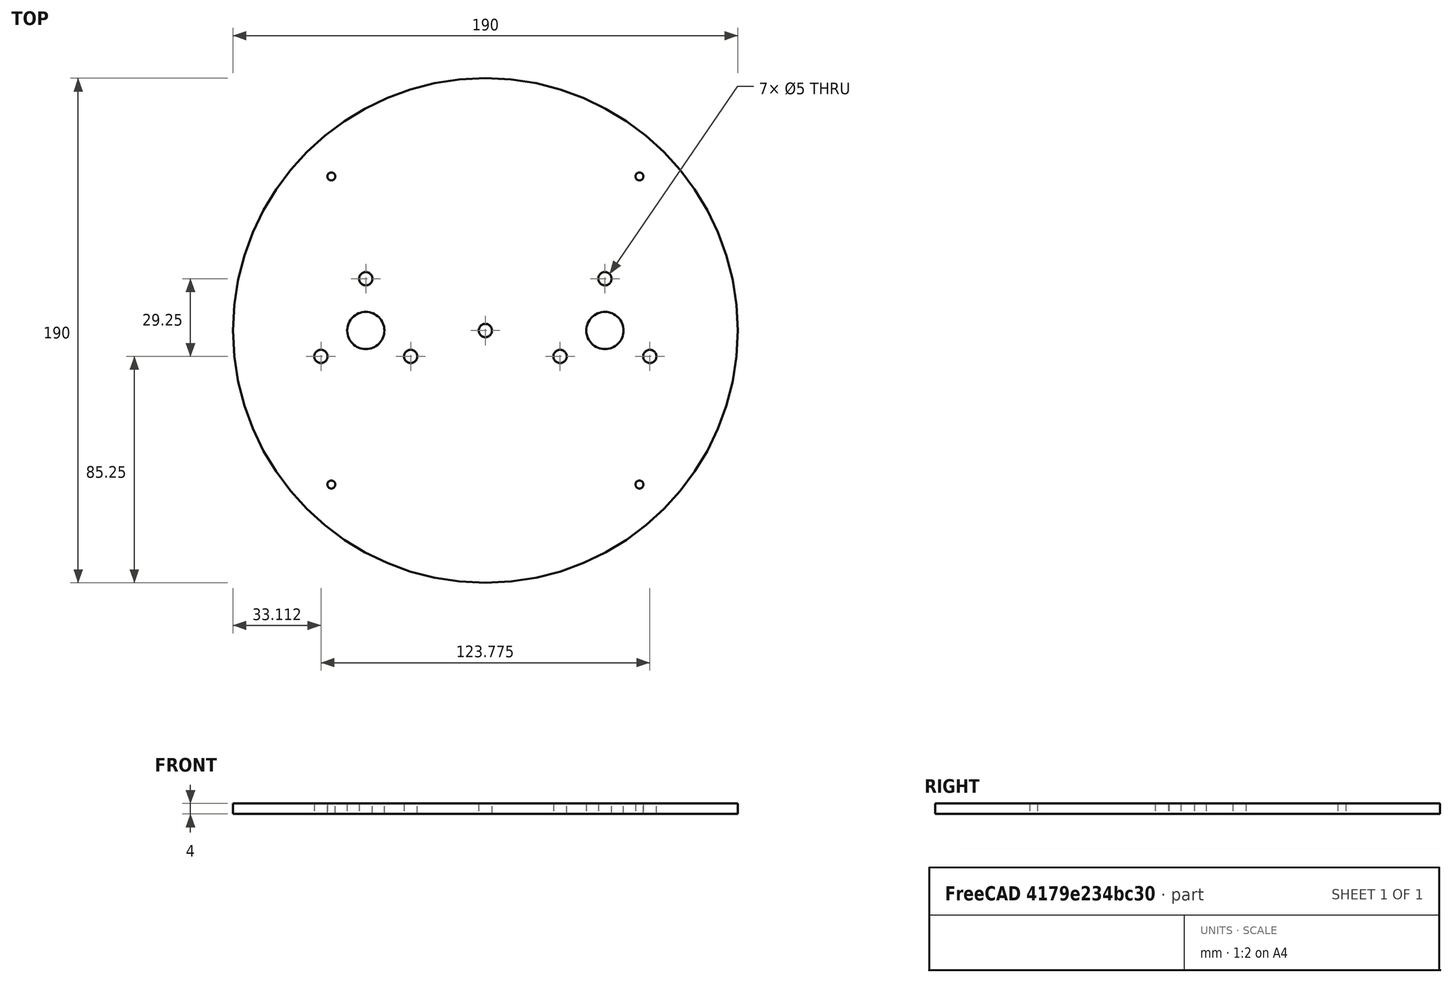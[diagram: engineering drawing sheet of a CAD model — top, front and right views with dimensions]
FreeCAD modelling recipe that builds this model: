
FCSTD DOCUMENT  (FreeCAD 0.19R24276 (Git))
Label: Osnovanie_karuseli
License: All rights reserved
LicenseURL: http://en.wikipedia.org/wiki/All_rights_reserved
objects: Sketcher::SketchObject×1, PartDesign::Pad×1, PartDesign::Body×1
note: 4 computed .brp shape members not serialized (recipe doc carries the construction recipe); baked Part::Feature solids carry a one-line shape summary decoded from their .brp

FEATURE [Sketcher::SketchObject] Sketch
  FullyConstrained = true
  MapMode = 5
  Support = -> [XY_Plane]
  sketch-geometry (27):
    g0: Circle CenterX=0 CenterY=0 CenterZ=0 NormalX=0 NormalY=0 NormalZ=1 AngleXU=0 Radius=95
    g1: Circle CenterX=-45 CenterY=0 CenterZ=0 NormalX=0 NormalY=0 NormalZ=1 AngleXU=0 Radius=7
    g2: Circle CenterX=45 CenterY=0 CenterZ=0 NormalX=0 NormalY=0 NormalZ=1 AngleXU=0 Radius=7
    g3: LineSegment StartX=0 StartY=0 StartZ=0 EndX=57.9828 EndY=57.9828 EndZ=0
    g4: LineSegment StartX=0 StartY=0 StartZ=0 EndX=-57.9828 EndY=57.9828 EndZ=0
    g5: LineSegment StartX=0 StartY=0 StartZ=0 EndX=-57.9828 EndY=-57.9828 EndZ=0
    g6: LineSegment StartX=0 StartY=0 StartZ=0 EndX=57.9828 EndY=-57.9828 EndZ=0
    g7: Circle CenterX=0 CenterY=0 CenterZ=0 NormalX=0 NormalY=0 NormalZ=1 AngleXU=0 Radius=82
    g8: Circle CenterX=57.9828 CenterY=57.9828 CenterZ=0 NormalX=0 NormalY=0 NormalZ=1 AngleXU=0 Radius=1.5
    g9: Circle CenterX=-57.9828 CenterY=57.9828 CenterZ=0 NormalX=0 NormalY=0 NormalZ=1 AngleXU=0 Radius=1.5
    g10: Circle CenterX=-57.9828 CenterY=-57.9828 CenterZ=0 NormalX=0 NormalY=0 NormalZ=1 AngleXU=0 Radius=1.5
    g11: Circle CenterX=57.9828 CenterY=-57.9828 CenterZ=0 NormalX=0 NormalY=0 NormalZ=1 AngleXU=0 Radius=1.5
    g12: LineSegment StartX=-45 StartY=19.5 StartZ=0 EndX=-61.8875 EndY=-9.75 EndZ=0
    g13: LineSegment StartX=-61.8875 StartY=-9.75 StartZ=0 EndX=-28.1125 EndY=-9.75 EndZ=0
    g14: LineSegment StartX=-28.1125 StartY=-9.75 StartZ=0 EndX=-45 EndY=19.5 EndZ=0
    g15: Circle CenterX=-45 CenterY=0 CenterZ=0 NormalX=0 NormalY=0 NormalZ=1 AngleXU=0 Radius=19.5
    g16: LineSegment StartX=45 StartY=19.5 StartZ=0 EndX=28.1125 EndY=-9.75 EndZ=0
    g17: LineSegment StartX=28.1125 StartY=-9.75 StartZ=0 EndX=61.8875 EndY=-9.75 EndZ=0
    g18: LineSegment StartX=61.8875 StartY=-9.75 StartZ=0 EndX=45 EndY=19.5 EndZ=0
    g19: Circle CenterX=45 CenterY=0 CenterZ=0 NormalX=0 NormalY=0 NormalZ=1 AngleXU=0 Radius=19.5
    g20: Circle CenterX=-45 CenterY=19.5 CenterZ=0 NormalX=0 NormalY=0 NormalZ=1 AngleXU=0 Radius=2.5
    g21: Circle CenterX=-28.1125 CenterY=-9.75 CenterZ=0 NormalX=0 NormalY=0 NormalZ=1 AngleXU=0 Radius=2.5
    g22: Circle CenterX=-61.8875 CenterY=-9.75 CenterZ=0 NormalX=0 NormalY=0 NormalZ=1 AngleXU=0 Radius=2.5
    g23: Circle CenterX=45 CenterY=19.5 CenterZ=0 NormalX=0 NormalY=0 NormalZ=1 AngleXU=0 Radius=2.5
    g24: Circle CenterX=28.1125 CenterY=-9.75 CenterZ=0 NormalX=0 NormalY=0 NormalZ=1 AngleXU=0 Radius=2.5
    g25: Circle CenterX=61.8875 CenterY=-9.75 CenterZ=0 NormalX=0 NormalY=0 NormalZ=1 AngleXU=0 Radius=2.5
    g26: Circle CenterX=0 CenterY=0 CenterZ=0 NormalX=0 NormalY=0 NormalZ=1 AngleXU=0 Radius=2.5
  constraints (62):
    c: Coincident(g0,g-1)
    c: Diameter(g0) = 190
    c: PointOnObject(g1,g-1)
    c: PointOnObject(g2,g-1)
    c: Diameter(g2) = 14
    c: Equal(g2,g1)
    c: DistanceX(g0,g2) = 45
    c: DistanceX(g1,g0) = 45
    c: Coincident(g3,g0)
    c: Coincident(g4,g0)
    c: Coincident(g5,g0)
    c: Coincident(g6,g0)
    c: Parallel(g3,g5)
    c: Parallel(g4,g6)
    c: Perpendicular(g3,g4)
    c: Angle(g-1,g3) = 0.785398
    c: Coincident(g7,g0)
    c: Diameter(g7) = 164
    c: PointOnObject(g3,g7)
    c: PointOnObject(g4,g7)
    c: PointOnObject(g5,g7)
    c: PointOnObject(g6,g7)
    c: Coincident(g8,g3)
    c: Coincident(g9,g4)
    c: Coincident(g10,g5)
    c: Coincident(g11,g6)
    c: Diameter(g8) = 3
    c: Equal(g8,g9)
    c: Equal(g8,g10)
    c: Equal(g8,g11)
    c: Coincident(g12,g13)
    c: Coincident(g13,g14)
    c: Coincident(g14,g12)
    c: Equal(g12,g13)
    c: Equal(g12,g14)
    c: PointOnObject(g12,g15)
    c: PointOnObject(g13,g15)
    c: PointOnObject(g14,g15)
    c: Coincident(g15,g1)
    c: Coincident(g16,g17)
    c: Coincident(g17,g18)
    c: Coincident(g18,g16)
    c: Equal(g16,g17)
    c: Equal(g16,g18)
    c: PointOnObject(g16,g19)
    c: PointOnObject(g17,g19)
    c: PointOnObject(g18,g19)
    c: Coincident(g19,g2)
    c: Horizontal(g13)
    c: Horizontal(g17)
    c: Diameter(g15) = 39
    c: Diameter(g19) = 39
    c: Coincident(g20,g12)
    c: Coincident(g21,g13)
    c: Coincident(g22,g12)
    c: Coincident(g23,g16)
    c: Coincident(g24,g16)
    c: Coincident(g25,g17)
    c: Diameter(g20) = 5
    c: Equal(g20, g21-g25) x5
    c: Coincident(g26,g0)
    c: Diameter(g26) = 5
FEATURE [PartDesign::Pad] Pad
  Direction = (1,1,1)
  Length = 4
  Length2 = 100
  Profile = -> Sketch
  Type = 0
FEATURE [PartDesign::Body] Body
  Group = -> [Sketch,Pad]
  Origin = -> Origin
  Tip = -> Pad
